FCSTD DOCUMENT  (FreeCAD 1.0RUnknown)
Label: quick-release
License: All rights reserved
LicenseURL: http://en.wikipedia.org/wiki/All_rights_reserved
objects: Sketcher::SketchObject×1, PartDesign::Body×1, Image::ImagePlane×1
note: 3 computed .brp shape members not serialized (recipe doc carries the construction recipe); baked Part::Feature solids carry a one-line shape summary decoded from their .brp

FEATURE [Sketcher::SketchObject] Sketch
  ArcFitTolerance = 1e-06
  AttachmentSupport = -> [XY_Plane]
  FullyConstrained = false
  MakeInternals = false
  MapMode = 5
  sketch-geometry (8):
    g0: LineSegment StartX=-6.48989 StartY=6.36238 StartZ=0 EndX=8.32666 EndY=6.36238 EndZ=0
    g1: LineSegment StartX=8.32666 StartY=6.36238 StartZ=0 EndX=8.32666 EndY=64.6893 EndZ=0
    g2: LineSegment StartX=8.32666 StartY=64.6893 StartZ=0 EndX=-6.48989 EndY=64.6893 EndZ=0
    g3: LineSegment StartX=-6.48989 StartY=64.6893 StartZ=0 EndX=-6.48989 EndY=6.36238 EndZ=0
    g4: LineSegment StartX=-12.8207 StartY=69.93 StartZ=0 EndX=-12.8207 EndY=0 EndZ=0
    g5: LineSegment StartX=-12.8207 StartY=0 StartZ=0 EndX=14.966 EndY=0 EndZ=0
    g6: LineSegment StartX=14.966 StartY=0 StartZ=0 EndX=14.966 EndY=69.93 EndZ=0
    g7: LineSegment StartX=14.966 StartY=69.93 StartZ=0 EndX=-12.8207 EndY=69.93 EndZ=0
  constraints (17):
    c: Coincident(g0,g1)
    c: Coincident(g1,g2)
    c: Coincident(g2,g3)
    c: Coincident(g3,g0)
    c: Horizontal(g0)
    c: Horizontal(g2)
    c: Vertical(g1)
    c: Vertical(g3)
    c: Coincident(g4,g5)
    c: Coincident(g5,g6)
    c: Coincident(g6,g7)
    c: Coincident(g7,g4)
    c: Vertical(g4)
    c: Vertical(g6)
    c: Horizontal(g5)
    c: Horizontal(g7)
    c: PointOnObject(g5,g-1)
FEATURE [PartDesign::Body] Body
  AllowCompound = false
  Group = -> [Sketch]
  Origin = -> Origin
FEATURE [Image::ImagePlane] quick_release_chest_harness  label="quick-release-chest-harness"
  XSize = 406.349
  YSize = 541.799
